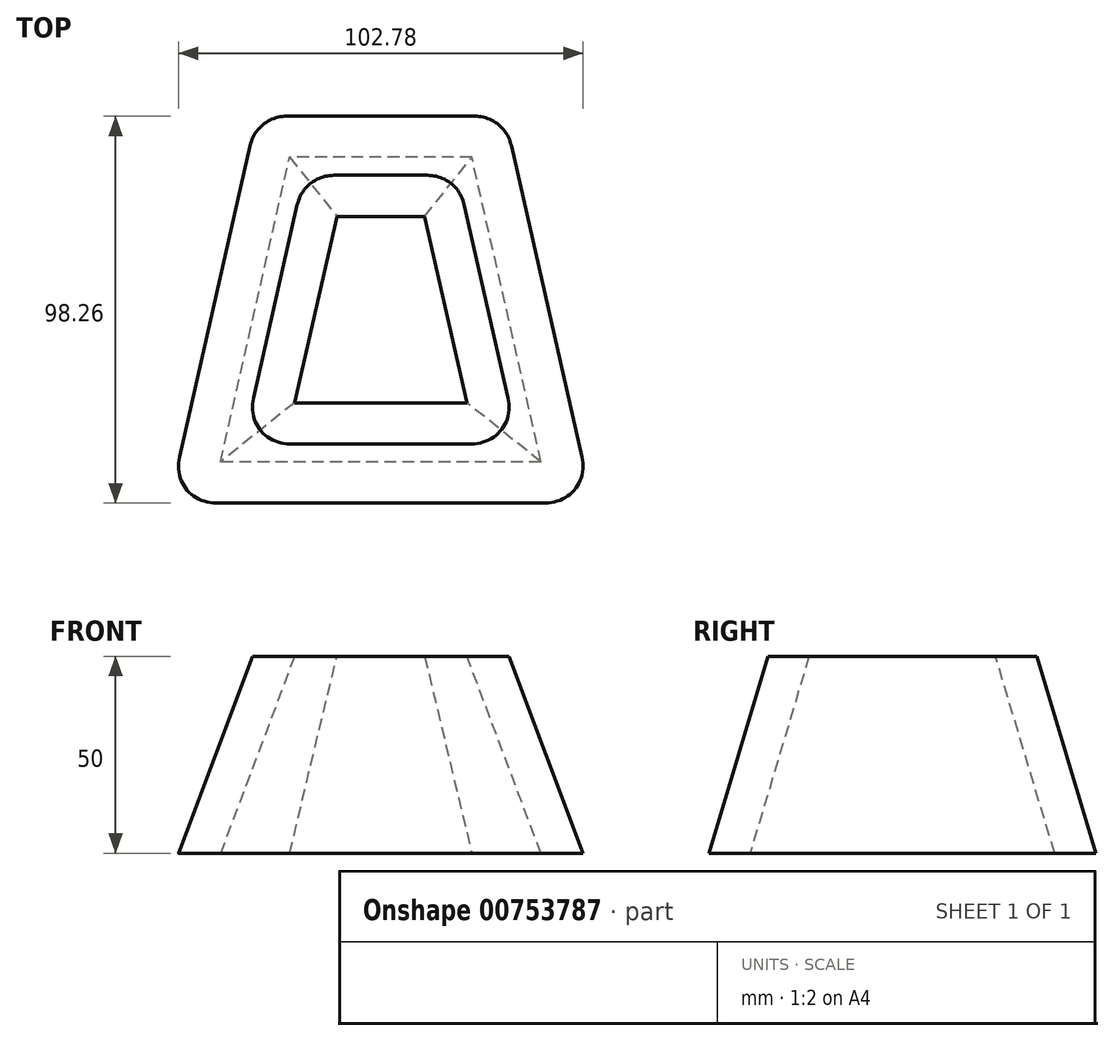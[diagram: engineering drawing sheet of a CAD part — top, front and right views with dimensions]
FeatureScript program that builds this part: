
annotation { "Feature Type Name" : "Feature", "Feature Type Description" : "" }
export const myFeature = defineFeature(function(context is Context, id is Id, definition is map)
    precondition{}
    {
        {
            var Q0;
            Q0=qCreatedBy(makeId("Top.planeOp"),FACE);
            var sketch = newSketch(context, id + "F0", { "sketchPlane" : qUnion([Q0])});
            skLineSegment(sketch, "E0", {"start": v(0, 0) * mm, "end": v(-19.5, 0) * mm});
            skLineSegment(sketch, "E1", {"start": v(0, 0) * mm, "end": v(0, -68.26) * mm, "construction": true});
            skLineSegment(sketch, "E2", {"start": v(-35, -68.26) * mm, "end": v(0, -68.26) * mm});
            skLineSegment(sketch, "E3", {"start": v(-35, -68.26) * mm, "end": v(-19.5, 0) * mm});
            skLineSegment(sketch, "E4.MirrorCS", {"start": v(0, 0) * mm, "end": v(19.5, 0) * mm});
            skLineSegment(sketch, "E5.MirrorCS", {"start": v(35, -68.26) * mm, "end": v(19.5, 0) * mm});
            skLineSegment(sketch, "E6.MirrorCS", {"start": v(35, -68.26) * mm, "end": v(0, -68.26) * mm});
            skSolve(sketch);
        }
        {
            var Q0;
            Q0=qCreatedBy(makeId("Top.planeOp"),FACE);
            cPlane(context, id + "F1", {"entities" : qUnion([Q0]), "cplaneType" : CPlaneType.OFFSET, "offset" : 50 * mm, "oppositeDirection" : true, "width" : 150 * mm, "height" : 150 * mm});
        }
        {
            var Q0;
            Q0=qCreatedBy(id+"F1.planeOp",FACE);
            var sketch = newSketch(context, id + "F2", { "sketchPlane" : qUnion([Q0])});
            skLineSegment(sketch, "E7.0", {"start": v(-35, -68.26) * mm, "end": v(-19.5, 0) * mm, "construction": true});
            skLineSegment(sketch, "E8.0", {"start": v(35, -68.26) * mm, "end": v(19.5, 0) * mm, "construction": true});
            skLineSegment(sketch, "E9.0", {"start": v(35, -68.26) * mm, "end": v(0, -68.26) * mm, "construction": true});
            skLineSegment(sketch, "E10.0", {"start": v(-35, -68.26) * mm, "end": v(0, -68.26) * mm, "construction": true});
            skLineSegment(sketch, "E11.0", {"start": v(0, 0) * mm, "end": v(-19.5, 0) * mm, "construction": true});
            skLineSegment(sketch, "E12.0", {"start": v(0, 0) * mm, "end": v(19.5, 0) * mm, "construction": true});
            skLineSegment(sketch, "E13.0", {"start": v(53.79, -83.26) * mm, "end": v(31.48, 15) * mm});
            skLineSegment(sketch, "E13.1", {"start": v(-53.79, -83.26) * mm, "end": v(0, -83.26) * mm});
            skLineSegment(sketch, "E13.2", {"start": v(-53.79, -83.26) * mm, "end": v(-31.48, 15) * mm});
            skLineSegment(sketch, "E13.3", {"start": v(53.79, -83.26) * mm, "end": v(0, -83.26) * mm});
            skLineSegment(sketch, "E13.4", {"start": v(0, 15) * mm, "end": v(-31.48, 15) * mm});
            skLineSegment(sketch, "E13.5", {"start": v(0, 15) * mm, "end": v(31.48, 15) * mm});
            skSolve(sketch);
        }
        {
            var Q0;
            Q0=makeQuery(id+"F0.imprint","IMPRINT",FACE,{"disambiguationData":[TD([[makeQuery(id+"F0.imprint","IMPRINT",EDGE,{"derivedFrom":sQuery(id+"F0.wireOp",EDGE,"E0")}),1.0]])]});
            var Q1;
            Q1=makeQuery(id+"F2.imprint","IMPRINT",FACE,{"disambiguationData":[TD([[makeQuery(id+"F2.imprint","IMPRINT",EDGE,{"derivedFrom":sQuery(id+"F2.wireOp",EDGE,"E13.0")}),1.0]])]});
            loft(context, id + "F3", {"sheetProfilesArray" : [{ "sheetProfileEntities" : qUnion([Q0]) }, { "sheetProfileEntities" : qUnion([Q1]) }]});
        }
        {
            var Q0;
            Q0=makeQuery(id+"F3.opLoft","CAP_FACE",FACE,{"disambiguationData":[OSD([makeQuery(id+"F0.imprint","IMPRINT",FACE,{"disambiguationData":[TD([[makeQuery(id+"F0.imprint","IMPRINT",EDGE,{"derivedFrom":sQuery(id+"F0.wireOp",EDGE,"E0")}),1.0]])]})])],"isStart":true});
            var Q1;
            Q1=makeQuery(id+"F3.opLoft","CAP_FACE",FACE,{"disambiguationData":[OSD([makeQuery(id+"F2.imprint","IMPRINT",FACE,{"disambiguationData":[TD([[makeQuery(id+"F2.imprint","IMPRINT",EDGE,{"derivedFrom":sQuery(id+"F2.wireOp",EDGE,"E13.0")}),1.0]])]})])],"isStart":true});
            shell(context, id + "F4", {"entities" : qUnion([Q0, Q1]), "thickness" : 10 * mm});
        }
        {
            var Q0;
            Q0=makeQuery(id+"F3.opLoft","SWEPT_EDGE",EDGE,{"disambiguationData":[OSD([sQuery(id+"F0.wireOp",EDGE,"E0"),sQuery(id+"F0.wireOp",EDGE,"E3"),sQuery(id+"F2.wireOp",EDGE,"E13.2"),sQuery(id+"F2.wireOp",EDGE,"E13.4")])]});
            var Q1;
            Q1=makeQuery(id+"F3.opLoft","SWEPT_EDGE",EDGE,{"disambiguationData":[OSD([sQuery(id+"F0.wireOp",EDGE,"E2"),sQuery(id+"F0.wireOp",EDGE,"E3"),sQuery(id+"F2.wireOp",EDGE,"E13.1"),sQuery(id+"F2.wireOp",EDGE,"E13.2")])]});
            var Q2;
            Q2=makeQuery(id+"F3.opLoft","SWEPT_EDGE",EDGE,{"disambiguationData":[OSD([sQuery(id+"F0.wireOp",EDGE,"E5.MirrorCS"),sQuery(id+"F0.wireOp",EDGE,"E6.MirrorCS"),sQuery(id+"F2.wireOp",EDGE,"E13.0"),sQuery(id+"F2.wireOp",EDGE,"E13.3")])]});
            var Q3;
            Q3=makeQuery(id+"F3.opLoft","SWEPT_EDGE",EDGE,{"disambiguationData":[OSD([sQuery(id+"F0.wireOp",EDGE,"E4.MirrorCS"),sQuery(id+"F0.wireOp",EDGE,"E5.MirrorCS"),sQuery(id+"F2.wireOp",EDGE,"E13.0"),sQuery(id+"F2.wireOp",EDGE,"E13.5")])]});
            fillet(context, id + "F5", {"entities" : qUnion([Q0, Q1, Q2, Q3]), "radius" : 10 * mm, "tangentPropagation" : true, "allowEdgeOverflow" : false});
        }
    });
